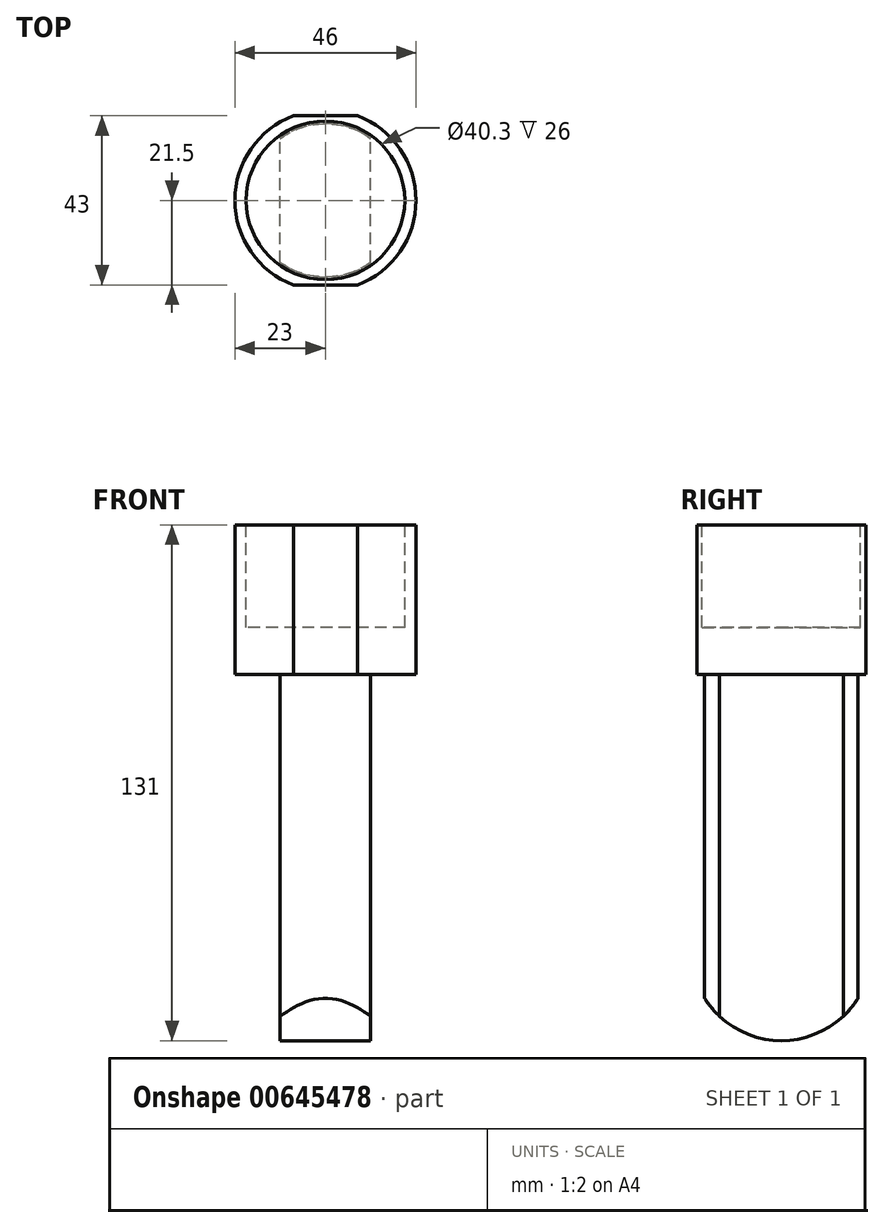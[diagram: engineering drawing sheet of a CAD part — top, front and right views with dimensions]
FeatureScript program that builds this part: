
annotation { "Feature Type Name" : "Feature", "Feature Type Description" : "" }
export const myFeature = defineFeature(function(context is Context, id is Id, definition is map)
    precondition{}
    {
        {
            var Q0;
            Q0=qCreatedBy(makeId("Top.planeOp"),FACE);
            var sketch = newSketch(context, id + "F0", { "sketchPlane" : qUnion([Q0])});
            skArc(sketch, "E0", {"start": v(-8.17, 21.5) * mm, "mid": v(-23, 0) * mm, "end": v(-8.17, -21.5) * mm});
            skLineSegment(sketch, "E1", {"start": v(-8.17, 21.5) * mm, "end": v(8.17, 21.5) * mm});
            skLineSegment(sketch, "E2.MirrorCS", {"start": v(-8.17, -21.5) * mm, "end": v(8.17, -21.5) * mm});
            skArc(sketch, "E3.trimOffspring", {"start": v(8.17, -21.5) * mm, "mid": v(23, 0) * mm, "end": v(8.17, 21.5) * mm});
            skSolve(sketch);
        }
        {
            var Q0;
            Q0=makeQuery(id+"F0.imprint","IMPRINT",FACE,{"disambiguationData":[TD([[makeQuery(id+"F0.imprint","IMPRINT",EDGE,{"derivedFrom":sQuery(id+"F0.wireOp",EDGE,"E0")}),1.0]])]});
            extrude(context, id + "F1", {"entities" : qUnion([Q0]), "depth" : 38 * mm, "offsetDistance" : 25 * mm});
        }
        {
            var Q0;
            Q0=makeQuery(id+"F1.opExtrude","CAP_FACE",FACE,{"disambiguationData":[OSD([sQuery(id+"F0.wireOp",EDGE,"E0"),sQuery(id+"F0.wireOp",EDGE,"E1"),sQuery(id+"F0.wireOp",EDGE,"E2.MirrorCS"),sQuery(id+"F0.wireOp",EDGE,"E3.trimOffspring")])],"isStart":false});
            var sketch = newSketch(context, id + "F2", { "sketchPlane" : qUnion([Q0])});
            skCircle(sketch, "E4", {"center": v(0, 0) * mm, "radius": 20.15 * mm});
            skSolve(sketch);
        }
        {
            var Q0;
            Q0 = qSketchRegion(id + "F2", true);
            extrude(context, id + "F3", {"entities" : qUnion([Q0]), "operationType" : NewBodyOperationType.REMOVE, "oppositeDirection" : true, "depth" : 26 * mm, "offsetDistance" : 25 * mm});
        }
        {
            var Q0;
            Q0=makeQuery(id+"F1.opExtrude","CAP_FACE",FACE,{"disambiguationData":[OSD([sQuery(id+"F0.wireOp",EDGE,"E0"),sQuery(id+"F0.wireOp",EDGE,"E1"),sQuery(id+"F0.wireOp",EDGE,"E2.MirrorCS"),sQuery(id+"F0.wireOp",EDGE,"E3.trimOffspring")])],"isStart":true});
            var sketch = newSketch(context, id + "F4", { "sketchPlane" : qUnion([Q0])});
            skArc(sketch, "E5", {"start": v(-11.5, -15.75) * mm, "mid": v(0, -19.5) * mm, "end": v(11.5, -15.75) * mm});
            skLineSegment(sketch, "E6", {"start": v(-11.5, 15.75) * mm, "end": v(-11.5, -15.75) * mm});
            skLineSegment(sketch, "E7", {"start": v(11.5, 15.75) * mm, "end": v(11.5, -15.75) * mm});
            skArc(sketch, "E8.trimOffspring", {"start": v(11.5, 15.75) * mm, "mid": v(0, 19.5) * mm, "end": v(-11.5, 15.75) * mm});
            skSolve(sketch);
        }
        {
            var Q0;
            Q0=makeQuery(id+"F4.imprint","IMPRINT",FACE,{"disambiguationData":[TD([[makeQuery(id+"F4.imprint","IMPRINT",EDGE,{"derivedFrom":sQuery(id+"F4.wireOp",EDGE,"E5")}),1.0]])]});
            extrude(context, id + "F5", {"entities" : qUnion([Q0]), "depth" : 93 * mm, "offsetDistance" : 25 * mm});
        }
        {
            var Q0;
            Q0=qCreatedBy(makeId("Right.planeOp"),FACE);
            var sketch = newSketch(context, id + "F6", { "sketchPlane" : qUnion([Q0])});
            skArc(sketch, "E9", {"start": v(-19.57, -82.08) * mm, "mid": v(0.09, -93) * mm, "end": v(19.66, -81.93) * mm});
            skLineSegment(sketch, "E10", {"start": v(-19.57, -82.08) * mm, "end": v(-30.96, -94.4) * mm});
            skLineSegment(sketch, "E11", {"start": v(-30.96, -94.4) * mm, "end": v(0, -104.06) * mm});
            skLineSegment(sketch, "E12", {"start": v(0, -104.06) * mm, "end": v(30.36, -99.92) * mm});
            skLineSegment(sketch, "E13", {"start": v(30.36, -99.92) * mm, "end": v(19.66, -81.93) * mm});
            skSolve(sketch);
        }
        {
            var Q0;
            Q0=makeQuery(id+"F6.imprint","IMPRINT",FACE,{"disambiguationData":[TD([[makeQuery(id+"F6.imprint","IMPRINT",EDGE,{"derivedFrom":sQuery(id+"F6.wireOp",EDGE,"E9")}),-1.0]])]});
            extrude(context, id + "F7", {"entities" : qUnion([Q0]), "operationType" : NewBodyOperationType.REMOVE, "endBound" : BoundingType.SYMMETRIC, "oppositeDirection" : true, "depth" : 25 * mm, "offsetDistance" : 25 * mm});
        }
    });
